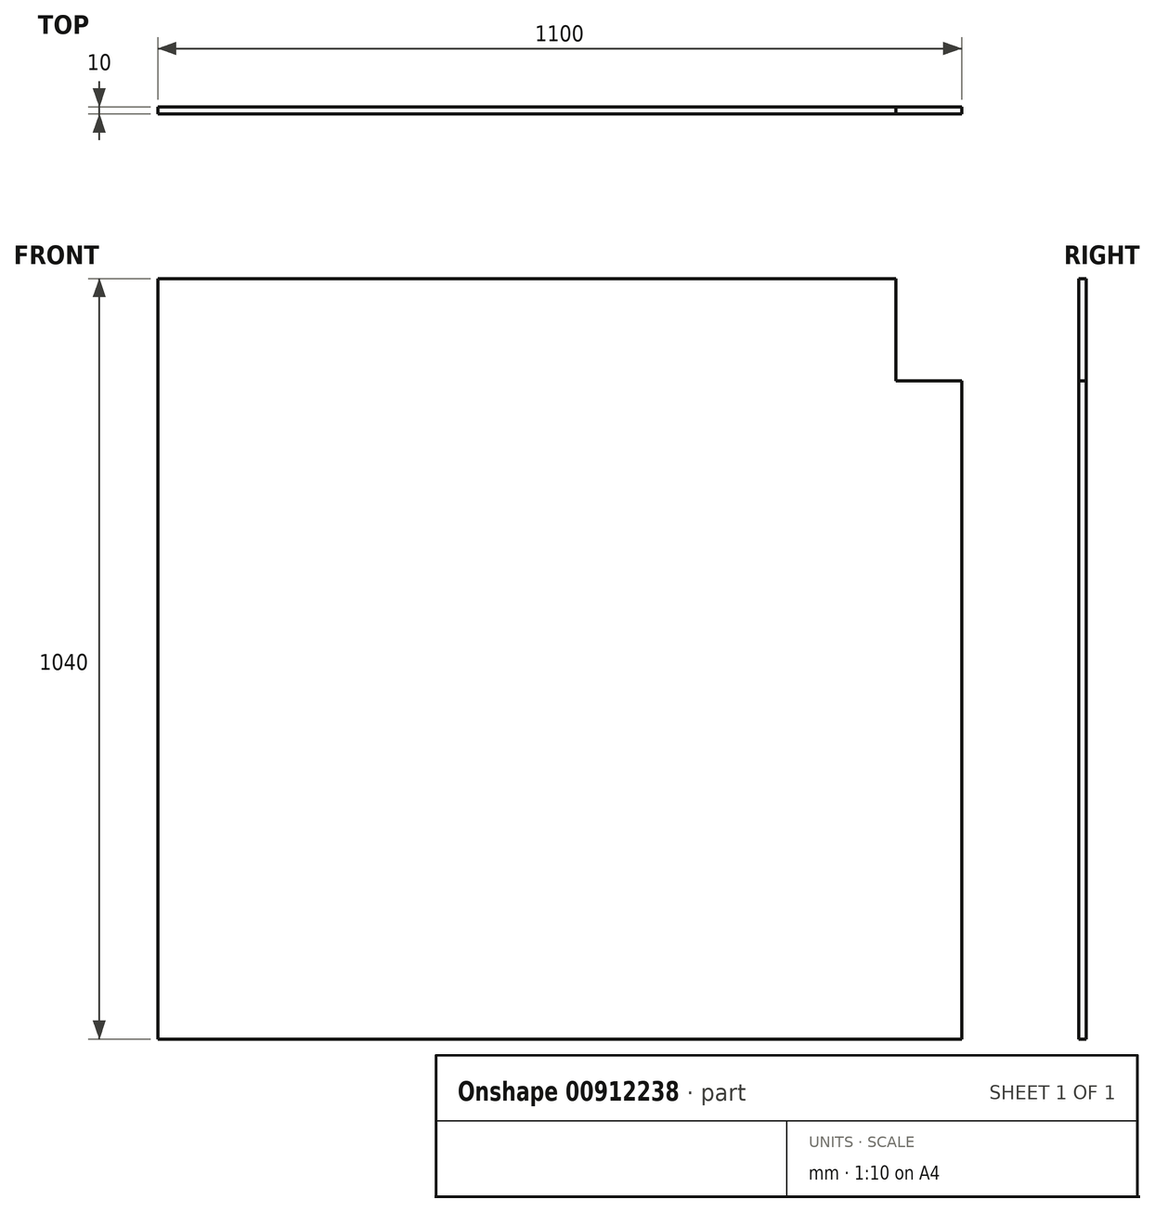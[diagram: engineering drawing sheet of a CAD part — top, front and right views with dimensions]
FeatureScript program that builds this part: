
annotation { "Feature Type Name" : "Feature", "Feature Type Description" : "" }
export const myFeature = defineFeature(function(context is Context, id is Id, definition is map)
    precondition{}
    {
        {
            var Q0;
            Q0=qCreatedBy(makeId("Front.planeOp"),FACE);
            var sketch = newSketch(context, id + "F0", { "sketchPlane" : qUnion([Q0])});
            skLineSegment(sketch, "E0.bottom", {"start": v(-611.45, 679.87) * mm, "end": v(398.55, 679.87) * mm});
            skLineSegment(sketch, "E0.top", {"start": v(-611.45, -360.13) * mm, "end": v(488.55, -360.13) * mm});
            skLineSegment(sketch, "E0.left", {"start": v(-611.45, 679.87) * mm, "end": v(-611.45, -360.13) * mm});
            skLineSegment(sketch, "E0.right", {"start": v(488.55, 539.87) * mm, "end": v(488.55, -360.13) * mm});
            skLineSegment(sketch, "E1", {"start": v(488.55, 539.87) * mm, "end": v(398.55, 539.87) * mm});
            skLineSegment(sketch, "E2", {"start": v(398.55, 539.87) * mm, "end": v(398.55, 679.87) * mm});
            skSolve(sketch);
        }
        {
            var Q0;
            Q0=qSketchRegion(id+"F0",true);
            extrude(context, id + "F1", {"entities" : qUnion([Q0]), "depth" : 10 * mm, "offsetDistance" : 25 * mm});
        }
    });
